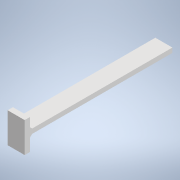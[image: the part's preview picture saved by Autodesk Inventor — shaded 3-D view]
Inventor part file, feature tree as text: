
AUTODESK INVENTOR PART (.ipt)
format: ipt  version: 2020 (Build 240168000, 168)  size: 125,952 bytes
history: native  units: mm
features: other x3, extrude x2, sketch x2, chamfer x1, thicken_offset x1, reference x1, projected_geometry x1
ambient origin geometry x8: Origin, YZ Plane, XZ Plane, XY Plane, X Axis, Y Axis, Z Axis, Center Point
bodies: Solid1 (feature_tree)
feature tree (11):
  extrude  "Extrusion1"  Depth=80.0mm
  extrude  "Extrusion2"  Depth=3.0mm TaperAngle=0.0deg
  chamfer  "Chamfer1"  Distance=1.0mm Angle=45.0deg
  thicken_offset  "Thicken1"
  sketch  "Sketch1"  dims[d0=80.0mm d1=0.0mm d2=8.0mm]
  reference  "Reference1"
  sketch  "Sketch2"  dims[d3=6.0mm d4=3.0mm d5=0.0mm d6=1.0mm d7=2.0mm d8=45.0deg d9=0.2mm d10=0.2mm]
  projected_geometry  "Projected Loop1"
  parser-record x1  (decoder bookkeeping rows leaked as tree rows — omitted from the tree; the rows remain in map.json)
  other  "motorized2.iam"
  other  "servo_bracket:1"
note: 1 file-system path scrubbed to <path> (originals preserved in map.json)
